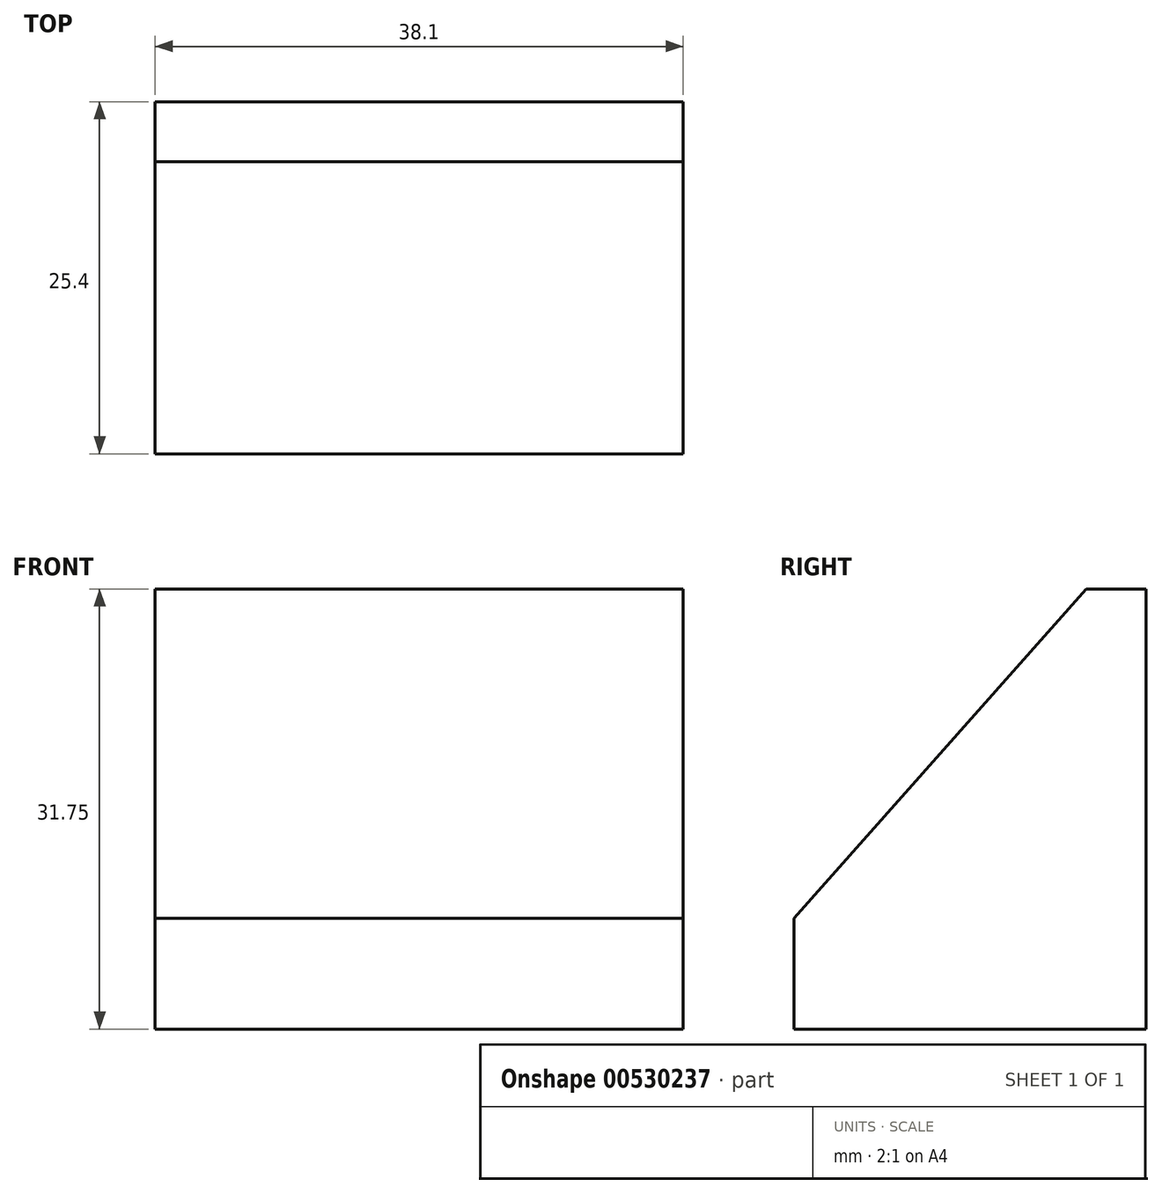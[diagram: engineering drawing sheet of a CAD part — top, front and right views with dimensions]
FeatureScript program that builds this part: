
annotation { "Feature Type Name" : "Feature", "Feature Type Description" : "" }
export const myFeature = defineFeature(function(context is Context, id is Id, definition is map)
    precondition{}
    {
        {
            var Q0;
            Q0=qCreatedBy(makeId("Front.planeOp"),FACE);
            var sketch = newSketch(context, id + "F0", { "sketchPlane" : qUnion([Q0])});
            skLineSegment(sketch, "E0", {"start": v(-50.52, 0) * mm, "end": v(-12.42, 0) * mm});
            skLineSegment(sketch, "E1", {"start": v(-12.42, 0) * mm, "end": v(-12.42, 31.75) * mm});
            skLineSegment(sketch, "E2", {"start": v(-12.42, 31.75) * mm, "end": v(-50.52, 31.75) * mm});
            skLineSegment(sketch, "E3", {"start": v(-50.52, 31.75) * mm, "end": v(-50.52, 0) * mm});
            skSolve(sketch);
        }
        {
            var Q0;
            Q0 = qSketchRegion(id + "F0", true);
            extrude(context, id + "F1", {"entities" : qUnion([Q0]), "depth" : 25.4 * mm, "offsetDistance" : 25.4 * mm});
        }
        {
            var Q0;
            Q0=makeQuery(id+"F1.opExtrude","SWEPT_FACE",FACE,{"disambiguationData":[OSD([sQuery(id+"F0.wireOp",EDGE,"E1")])]});
            var sketch = newSketch(context, id + "F2", { "sketchPlane" : qUnion([Q0])});
            skLineSegment(sketch, "E4", {"start": v(-4.34, 31.75) * mm, "end": v(-25.4, 8) * mm});
            skLineSegment(sketch, "E5", {"start": v(-25.4, 8) * mm, "end": v(-4.34, 31.75) * mm});
            skLineSegment(sketch, "E6", {"start": v(-25.4, 8) * mm, "end": v(-25.4, 31.75) * mm});
            skLineSegment(sketch, "E7", {"start": v(-25.4, 31.75) * mm, "end": v(-4.34, 31.75) * mm});
            skSolve(sketch);
        }
        {
            var Q0;
            Q0 = qSketchRegion(id + "F2", true);
            extrude(context, id + "F3", {"entities" : qUnion([Q0]), "operationType" : NewBodyOperationType.REMOVE, "endBound" : BoundingType.THROUGH_ALL, "oppositeDirection" : true, "depth" : 12.7 * mm, "offsetDistance" : 25.4 * mm});
        }
        {
            var Q0;
            Q0 = qSketchRegion(id + "F2", true);
            extrude(context, id + "F4", {"entities" : qUnion([Q0]), "operationType" : NewBodyOperationType.REMOVE, "oppositeDirection" : true, "depth" : 25.4 * mm, "offsetDistance" : 25.4 * mm});
        }
    });
